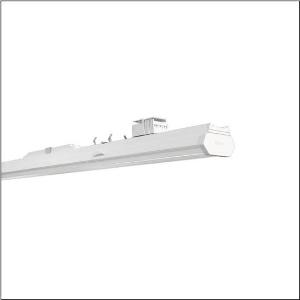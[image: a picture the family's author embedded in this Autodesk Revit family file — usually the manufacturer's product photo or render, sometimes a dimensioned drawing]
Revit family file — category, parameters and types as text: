
# Revit family: licross_r__21_protected_ho_52tp12cn4cxm_7b7d
name_source: partatom
category: Lighting Fixtures
units: mm (PartAtom-declared; Revit-internal decimal feet)

## family parameters
Cut with Voids When Loaded = No
Host = Face
Light Source = No
Part Type = Normal
Room Calculation Point = No
Round Connector Dimension = Use Diameter
Shared = No

## types (1)
- --- (1 x LED, 12460 lm, 68.9 W, 4000K)
    Apparent Load = 69 VA
    CIE Flux Codes = 70 91 97 98 100
    Color Rendering = 80
    Color Temperature = 4000K
    Default Elevation = 1800 mm
    Description = Licross® 21 Protected HO, luminaire insert, of sheet steel, galvanised, coil coated, white, length: 1.500mm, width: 90mm, height: 103mm, LED rated luminous flux: 12.460lm, light colour: 840, SDCM (Standard Deviation of Colour Matching)MacAdam ≤ 3 SDCM (initial), control gear: ON/OFF Multilumen, CLOi, with plug, 3-pole, with phase selection, mains connection: 220..240V, AC, 50/60Hz, start of lifetime: 69W, end of service life: 83W, internal wiring halogen-free, primary light control with lens, of plastic, primary optical cover: cover, of PMMA, light emission: direct distribution, primary light characteristic: symmetric, protection rating (complete): IP64, insulation class (complete): insulation class I (protective earthing), certification: CE, ENEC, VDE, UKCA, protection symbol: D if used in an environment with conductive dust loads with corresponding accessories, impact resistance: IK06, permissible ambient temperature for indoor applications: -35..+35°C, corresponds to IFS (International Featured Standards) requirements for safety and quality in the food industry, reducing of maximum allowable ambient temperature of 5°C with ceiling mounting, LABS conformity tested according to VDMA 24364:2018-05, packaging unit: 1 piece
    Height = 92 mm
    Lamp = 1 x LED
    Lamp Light Flux = 12460 lm
    Lamp Power = 68.9 W
    Lamp count = 1
    Length = 1500 mm
    Luminous efficacy = 181 lm/W
    Manufacturer = Siteco
    ModVariant = No
    Model = 52TP12CN4CXM
    Mounting Place = Ceiling
    Mounting Type = Pendant
    Number of Poles = 1
    OnlyDefault = Yes
    Power Factor = 1
    Product Name = Licross® 21 Protected HO
    Product group = luminaire insert | ceiling pendant
    ProductGroupID = 901
    Protection Class = Protection class I
    Protection Degree = IP 64
    RLX_Detail_Level = 1
    RLX_Emergency_Light_Flux = 0 lm
    RLX_Emergency_Type = 0
    RLX_Emergency_Type_DB = No
    RlxData = <blob elided: 22173 chars, md5=10a0a3f5>
    Socket = socket
    Standby Power = 0 W
    System Light Flux = 12460 lm
    System Power = 69 W
    Type Comments = factory setting: luminous flux: 100 % | (A | C | E) | 162 mA
    Type Image = l_1256148.jpg
    URL = http://relux.com
    VarID = @adj_115391
    Voltage = 0 V
    Weight = 0.00 kg
    Width = 88 mm

## geometry (parser evidence)
native form markers: Blend x4, Sweep x11
no freeform markers — native parametric forms only
